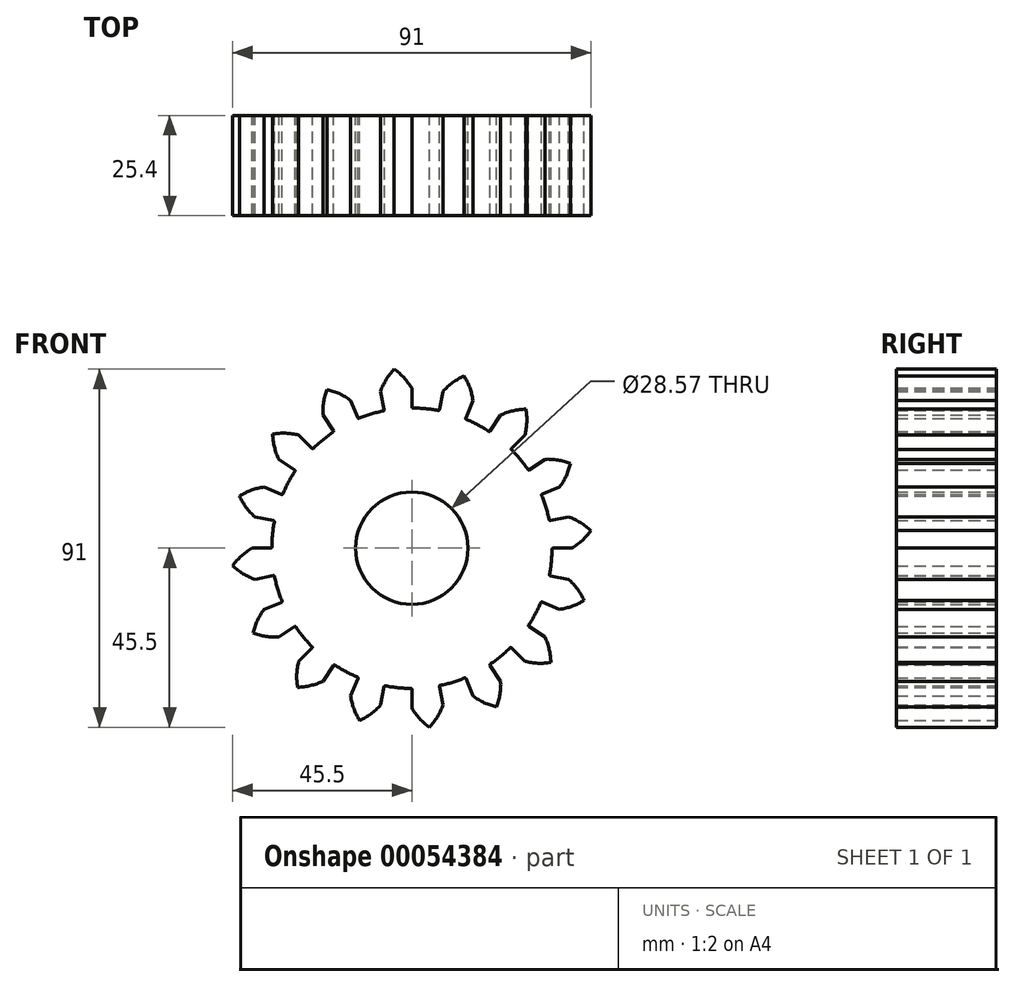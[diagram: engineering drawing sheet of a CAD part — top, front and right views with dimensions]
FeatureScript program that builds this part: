
annotation { "Feature Type Name" : "Feature", "Feature Type Description" : "" }
export const myFeature = defineFeature(function(context is Context, id is Id, definition is map)
    precondition{}
    {
        {
            var Q0;
            Q0=qCreatedBy(makeId("Front.planeOp"),FACE);
            var sketch = newSketch(context, id + "F0", { "sketchPlane" : qUnion([Q0])});
            skArc(sketch, "E0", {"start": v(-29.7, 19.55) * mm, "mid": v(-31.36, 16.76) * mm, "end": v(-32.76, 13.84) * mm});
            skLineSegment(sketch, "E1", {"start": v(-6.94, 34.88) * mm, "end": v(-7.93, 39.86) * mm, "construction": true});
            skArc(sketch, "E2.trimOffspring", {"start": v(0, 40.64) * mm, "mid": v(-1.98, 43.3) * mm, "end": v(-4.48, 45.5) * mm});
            skLineSegment(sketch, "E3.trimOffspring", {"start": v(0, 35.56) * mm, "end": v(0, 40.64) * mm, "construction": true});
            skPoint(sketch, "E4.orphan", {"position": v(0, 72.8) * mm});
            skPoint(sketch, "E5.trimOffspring.end.orphan", {"position": v(-14.48, 72.8) * mm});
            skPoint(sketch, "E6.orphan", {"position": v(-81.45, 40.64) * mm});
            skPoint(sketch, "E7.orphan", {"position": v(-81.45, 11) * mm});
            skArc(sketch, "E8", {"start": v(-20, 29.47) * mm, "mid": v(-22.6, 27.53) * mm, "end": v(-25, 25.36) * mm});
            skLineSegment(sketch, "E9", {"start": v(0, 40.64) * mm, "end": v(0, 35.56) * mm});
            skArc(sketch, "E10.MirrorCS", {"start": v(-7.93, 39.86) * mm, "mid": v(-6.5, 42.86) * mm, "end": v(-4.48, 45.5) * mm});
            skLineSegment(sketch, "E11.MirrorCS", {"start": v(-7.93, 39.86) * mm, "end": v(-6.94, 34.88) * mm});
            skLineSegment(sketch, "E12.trimOffspring", {"start": v(-7.63, 40.64) * mm, "end": v(-8.08, 40.64) * mm, "construction": true});
            skLineSegment(sketch, "E13", {"start": v(-7.93, 39.86) * mm, "end": v(-7, 35.18) * mm});
            skLineSegment(sketch, "E14", {"start": v(0, 40.64) * mm, "end": v(0, 35.87) * mm});
            skArc(sketch, "E15.1.0", {"start": v(-15.55, 37.55) * mm, "mid": v(-18.4, 39.25) * mm, "end": v(-21.55, 40.32) * mm});
            skLineSegment(sketch, "E15.1.1", {"start": v(-15.55, 37.55) * mm, "end": v(-13.73, 33.14) * mm});
            skLineSegment(sketch, "E15.1.2", {"start": v(-22.58, 33.8) * mm, "end": v(-19.93, 29.82) * mm});
            skArc(sketch, "E15.1.3", {"start": v(-22.58, 33.8) * mm, "mid": v(-22.4, 37.11) * mm, "end": v(-21.55, 40.32) * mm});
            skArc(sketch, "E15.2.0", {"start": v(-28.74, 28.74) * mm, "mid": v(-32.03, 29.22) * mm, "end": v(-35.34, 29) * mm});
            skLineSegment(sketch, "E15.2.1", {"start": v(-28.74, 28.74) * mm, "end": v(-25.36, 25.36) * mm});
            skLineSegment(sketch, "E15.2.2", {"start": v(-33.8, 22.58) * mm, "end": v(-29.78, 19.9) * mm});
            skArc(sketch, "E15.2.3", {"start": v(-33.8, 22.58) * mm, "mid": v(-34.9, 25.7) * mm, "end": v(-35.34, 29) * mm});
            skArc(sketch, "E15.3.0", {"start": v(-37.55, 15.55) * mm, "mid": v(-40.77, 14.74) * mm, "end": v(-43.75, 13.27) * mm});
            skLineSegment(sketch, "E15.3.1", {"start": v(-37.55, 15.55) * mm, "end": v(-33.09, 13.7) * mm});
            skLineSegment(sketch, "E15.3.2", {"start": v(-39.86, 7.93) * mm, "end": v(-35.12, 6.99) * mm});
            skArc(sketch, "E15.3.3", {"start": v(-39.86, 7.93) * mm, "mid": v(-42.09, 10.4) * mm, "end": v(-43.75, 13.27) * mm});
            skArc(sketch, "E15.4.0", {"start": v(-40.64, 0) * mm, "mid": v(-43.3, -1.98) * mm, "end": v(-45.5, -4.48) * mm});
            skLineSegment(sketch, "E15.4.1", {"start": v(-40.64, 0) * mm, "end": v(-35.81, 0) * mm});
            skLineSegment(sketch, "E15.4.2", {"start": v(-39.86, -7.93) * mm, "end": v(-35.12, -6.99) * mm});
            skArc(sketch, "E15.4.3", {"start": v(-39.86, -7.93) * mm, "mid": v(-42.86, -6.5) * mm, "end": v(-45.5, -4.48) * mm});
            skArc(sketch, "E15.5.0", {"start": v(-37.55, -15.55) * mm, "mid": v(-39.25, -18.4) * mm, "end": v(-40.32, -21.55) * mm});
            skLineSegment(sketch, "E15.5.1", {"start": v(-37.55, -15.55) * mm, "end": v(-33.14, -13.73) * mm});
            skLineSegment(sketch, "E15.5.2", {"start": v(-33.8, -22.58) * mm, "end": v(-29.82, -19.93) * mm});
            skArc(sketch, "E15.5.3", {"start": v(-33.8, -22.58) * mm, "mid": v(-37.11, -22.4) * mm, "end": v(-40.32, -21.55) * mm});
            skArc(sketch, "E15.6.0", {"start": v(-28.74, -28.74) * mm, "mid": v(-29.22, -32.03) * mm, "end": v(-29, -35.34) * mm});
            skLineSegment(sketch, "E15.6.1", {"start": v(-28.74, -28.74) * mm, "end": v(-25.32, -25.32) * mm});
            skLineSegment(sketch, "E15.6.2", {"start": v(-22.58, -33.8) * mm, "end": v(-19.9, -29.78) * mm});
            skArc(sketch, "E15.6.3", {"start": v(-22.58, -33.8) * mm, "mid": v(-25.7, -34.9) * mm, "end": v(-29, -35.34) * mm});
            skArc(sketch, "E15.7.0", {"start": v(-15.55, -37.55) * mm, "mid": v(-14.74, -40.77) * mm, "end": v(-13.27, -43.75) * mm});
            skLineSegment(sketch, "E15.7.1", {"start": v(-15.55, -37.55) * mm, "end": v(-13.7, -33.09) * mm});
            skLineSegment(sketch, "E15.7.2", {"start": v(-7.93, -39.86) * mm, "end": v(-7, -35.18) * mm});
            skArc(sketch, "E15.7.3", {"start": v(-7.93, -39.86) * mm, "mid": v(-10.4, -42.09) * mm, "end": v(-13.27, -43.75) * mm});
            skArc(sketch, "E15.8.0", {"start": v(0, -40.64) * mm, "mid": v(1.98, -43.3) * mm, "end": v(4.48, -45.5) * mm});
            skLineSegment(sketch, "E15.8.1", {"start": v(0, -40.64) * mm, "end": v(0, -35.87) * mm});
            skLineSegment(sketch, "E15.8.2", {"start": v(7.93, -39.86) * mm, "end": v(7, -35.18) * mm});
            skArc(sketch, "E15.8.3", {"start": v(7.93, -39.86) * mm, "mid": v(6.5, -42.86) * mm, "end": v(4.48, -45.5) * mm});
            skArc(sketch, "E15.9.0", {"start": v(15.55, -37.55) * mm, "mid": v(18.4, -39.25) * mm, "end": v(21.55, -40.32) * mm});
            skLineSegment(sketch, "E15.9.1", {"start": v(15.55, -37.55) * mm, "end": v(13.73, -33.14) * mm});
            skLineSegment(sketch, "E15.9.2", {"start": v(22.58, -33.8) * mm, "end": v(19.9, -29.78) * mm});
            skArc(sketch, "E15.9.3", {"start": v(22.58, -33.8) * mm, "mid": v(22.4, -37.11) * mm, "end": v(21.55, -40.32) * mm});
            skArc(sketch, "E15.10.0", {"start": v(28.74, -28.74) * mm, "mid": v(32.03, -29.22) * mm, "end": v(35.34, -29) * mm});
            skLineSegment(sketch, "E15.10.1", {"start": v(28.74, -28.74) * mm, "end": v(25.32, -25.32) * mm});
            skLineSegment(sketch, "E15.10.2", {"start": v(33.8, -22.58) * mm, "end": v(29.78, -19.9) * mm});
            skArc(sketch, "E15.10.3", {"start": v(33.8, -22.58) * mm, "mid": v(34.9, -25.7) * mm, "end": v(35.34, -29) * mm});
            skArc(sketch, "E15.11.0", {"start": v(37.55, -15.55) * mm, "mid": v(40.77, -14.74) * mm, "end": v(43.75, -13.27) * mm});
            skLineSegment(sketch, "E15.11.1", {"start": v(37.55, -15.55) * mm, "end": v(33.09, -13.7) * mm});
            skLineSegment(sketch, "E15.11.2", {"start": v(39.86, -7.93) * mm, "end": v(35.18, -7) * mm});
            skArc(sketch, "E15.11.3", {"start": v(39.86, -7.93) * mm, "mid": v(42.09, -10.4) * mm, "end": v(43.75, -13.27) * mm});
            skArc(sketch, "E15.12.0", {"start": v(40.64, 0) * mm, "mid": v(43.3, 1.98) * mm, "end": v(45.5, 4.48) * mm});
            skLineSegment(sketch, "E15.12.1", {"start": v(40.64, 0) * mm, "end": v(35.87, 0) * mm});
            skLineSegment(sketch, "E15.12.2", {"start": v(39.86, 7.93) * mm, "end": v(35.18, 7) * mm});
            skArc(sketch, "E15.12.3", {"start": v(39.86, 7.93) * mm, "mid": v(42.86, 6.5) * mm, "end": v(45.5, 4.48) * mm});
            skArc(sketch, "E15.13.0", {"start": v(37.55, 15.55) * mm, "mid": v(39.25, 18.4) * mm, "end": v(40.32, 21.55) * mm});
            skLineSegment(sketch, "E15.13.1", {"start": v(37.55, 15.55) * mm, "end": v(33.14, 13.73) * mm});
            skLineSegment(sketch, "E15.13.2", {"start": v(33.8, 22.58) * mm, "end": v(29.82, 19.93) * mm});
            skArc(sketch, "E15.13.3", {"start": v(33.8, 22.58) * mm, "mid": v(37.11, 22.4) * mm, "end": v(40.32, 21.55) * mm});
            skArc(sketch, "E15.14.0", {"start": v(28.74, 28.74) * mm, "mid": v(29.22, 32.03) * mm, "end": v(29, 35.34) * mm});
            skLineSegment(sketch, "E15.14.1", {"start": v(28.74, 28.74) * mm, "end": v(25.32, 25.32) * mm});
            skLineSegment(sketch, "E15.14.2", {"start": v(22.58, 33.8) * mm, "end": v(19.9, 29.78) * mm});
            skArc(sketch, "E15.14.3", {"start": v(22.58, 33.8) * mm, "mid": v(25.7, 34.9) * mm, "end": v(29, 35.34) * mm});
            skArc(sketch, "E15.15.0", {"start": v(15.55, 37.55) * mm, "mid": v(14.74, 40.77) * mm, "end": v(13.27, 43.75) * mm});
            skLineSegment(sketch, "E15.15.1", {"start": v(15.55, 37.55) * mm, "end": v(13.7, 33.09) * mm});
            skLineSegment(sketch, "E15.15.2", {"start": v(7.93, 39.86) * mm, "end": v(7, 35.18) * mm});
            skArc(sketch, "E15.15.3", {"start": v(7.93, 39.86) * mm, "mid": v(10.4, 42.09) * mm, "end": v(13.27, 43.75) * mm});
            skArc(sketch, "E16.trimOffspring", {"start": v(-29.61, 19.79) * mm, "mid": v(-31.41, 16.79) * mm, "end": v(-32.9, 13.63) * mm});
            skArc(sketch, "E17.trimOffspring", {"start": v(-34.93, 6.69) * mm, "mid": v(-35.39, 3.49) * mm, "end": v(-35.56, 0.25) * mm});
            skArc(sketch, "E18.trimOffspring", {"start": v(-34.93, 6.95) * mm, "mid": v(-35.45, 3.5) * mm, "end": v(-35.62, 0) * mm});
            skArc(sketch, "E19.trimOffspring", {"start": v(-7.2, 34.88) * mm, "mid": v(-10.34, 34.08) * mm, "end": v(-13.4, 33) * mm});
            skArc(sketch, "E20.trimOffspring", {"start": v(6.7, 34.98) * mm, "mid": v(3.5, 35.45) * mm, "end": v(0.25, 35.62) * mm});
            skArc(sketch, "E21.trimOffspring", {"start": v(6.94, 34.88) * mm, "mid": v(3.49, 35.39) * mm, "end": v(0, 35.56) * mm});
            skArc(sketch, "E22.trimOffspring", {"start": v(19.79, 29.61) * mm, "mid": v(16.79, 31.41) * mm, "end": v(13.63, 32.9) * mm});
            skArc(sketch, "E23.trimOffspring", {"start": v(19.55, 29.7) * mm, "mid": v(16.76, 31.36) * mm, "end": v(13.84, 32.76) * mm});
            skArc(sketch, "E24.trimOffspring", {"start": v(29.47, 20) * mm, "mid": v(27.45, 22.7) * mm, "end": v(25.18, 25.18) * mm});
            skArc(sketch, "E25.trimOffspring", {"start": v(34.88, 7.2) * mm, "mid": v(34.08, 10.34) * mm, "end": v(33, 13.4) * mm});
            skArc(sketch, "E26.trimOffspring", {"start": v(29.57, 19.76) * mm, "mid": v(27.57, 22.46) * mm, "end": v(25.32, 24.97) * mm});
            skArc(sketch, "E27.trimOffspring", {"start": v(34.88, 6.94) * mm, "mid": v(34.03, 10.32) * mm, "end": v(32.85, 13.6) * mm});
            skArc(sketch, "E28.trimOffspring", {"start": v(34.98, -6.7) * mm, "mid": v(35.45, -3.5) * mm, "end": v(35.62, -0.25) * mm});
            skArc(sketch, "E29.trimOffspring", {"start": v(34.88, -6.94) * mm, "mid": v(35.39, -3.49) * mm, "end": v(35.56, 0) * mm});
            skArc(sketch, "E30.trimOffspring", {"start": v(29.7, -19.55) * mm, "mid": v(31.36, -16.76) * mm, "end": v(32.76, -13.84) * mm});
            skArc(sketch, "E31.trimOffspring", {"start": v(19.97, -29.43) * mm, "mid": v(22.56, -27.49) * mm, "end": v(24.97, -25.32) * mm});
            skArc(sketch, "E32.trimOffspring", {"start": v(7.2, -34.88) * mm, "mid": v(10.34, -34.08) * mm, "end": v(13.4, -33) * mm});
            skArc(sketch, "E33.trimOffspring", {"start": v(6.94, -34.88) * mm, "mid": v(10.32, -34.03) * mm, "end": v(13.6, -32.85) * mm});
            skArc(sketch, "E34.trimOffspring", {"start": v(-6.7, -34.98) * mm, "mid": v(-3.5, -35.45) * mm, "end": v(-0.25, -35.62) * mm});
            skArc(sketch, "E35.trimOffspring", {"start": v(-6.94, -34.88) * mm, "mid": v(-3.49, -35.39) * mm, "end": v(0, -35.56) * mm});
            skArc(sketch, "E36.trimOffspring", {"start": v(-19.55, -29.7) * mm, "mid": v(-16.76, -31.36) * mm, "end": v(-13.84, -32.76) * mm});
            skArc(sketch, "E37.trimOffspring", {"start": v(-29.47, -20) * mm, "mid": v(-27.45, -22.7) * mm, "end": v(-25.18, -25.18) * mm});
            skArc(sketch, "E38.trimOffspring", {"start": v(-29.57, -19.76) * mm, "mid": v(-27.57, -22.46) * mm, "end": v(-25.32, -24.97) * mm});
            skArc(sketch, "E39.trimOffspring", {"start": v(-34.83, -7.18) * mm, "mid": v(-34, -10.44) * mm, "end": v(-32.85, -13.6) * mm});
            skArc(sketch, "E40.trimOffspring", {"start": v(-34.93, -6.95) * mm, "mid": v(-34.12, -10.22) * mm, "end": v(-33, -13.4) * mm});
            skPoint(sketch, "E41.newPointA", {"position": v(-25.14, 25.14) * mm});
            skArc(sketch, "E41.filletArc", {"start": v(-25.36, 25.36) * mm, "mid": v(-25.19, 25.29) * mm, "end": v(-25, 25.36) * mm});
            skPoint(sketch, "E42.visualSharp", {"position": v(-29.57, 19.76) * mm});
            skArc(sketch, "E42.filletArc", {"start": v(-29.7, 19.55) * mm, "mid": v(-29.67, 19.74) * mm, "end": v(-29.78, 19.9) * mm});
            skPoint(sketch, "E43.visualSharp", {"position": v(-32.85, 13.6) * mm});
            skArc(sketch, "E43.filletArc", {"start": v(-33.09, 13.7) * mm, "mid": v(-32.9, 13.7) * mm, "end": v(-32.76, 13.84) * mm});
            skPoint(sketch, "E44.visualSharp", {"position": v(-34.88, 6.94) * mm});
            skArc(sketch, "E44.filletArc", {"start": v(-34.93, 6.69) * mm, "mid": v(-34.96, 6.88) * mm, "end": v(-35.12, 6.99) * mm});
            skPoint(sketch, "E45.visualSharp", {"position": v(-35.56, 0) * mm});
            skArc(sketch, "E45.filletArc", {"start": v(-35.81, 0) * mm, "mid": v(-35.63, 0.07) * mm, "end": v(-35.56, 0.25) * mm});
            skPoint(sketch, "E46.visualSharp", {"position": v(-34.88, -6.94) * mm});
            skArc(sketch, "E46.filletArc", {"start": v(-34.83, -7.18) * mm, "mid": v(-34.94, -7.02) * mm, "end": v(-35.12, -6.99) * mm});
            skPoint(sketch, "E47.newPointB", {"position": v(-32.85, -13.6) * mm});
            skArc(sketch, "E47.filletArc", {"start": v(-33.14, -13.73) * mm, "mid": v(-33, -13.6) * mm, "end": v(-33, -13.4) * mm});
            skPoint(sketch, "E48.newPointA", {"position": v(-29.57, -19.76) * mm});
            skArc(sketch, "E48.filletArc", {"start": v(-29.47, -20) * mm, "mid": v(-29.64, -19.9) * mm, "end": v(-29.82, -19.93) * mm});
            skPoint(sketch, "E49.visualSharp", {"position": v(-25.14, -25.14) * mm});
            skArc(sketch, "E49.filletArc", {"start": v(-25.32, -25.32) * mm, "mid": v(-25.25, -25.14) * mm, "end": v(-25.32, -24.97) * mm});
            skPoint(sketch, "E50.visualSharp", {"position": v(-19.76, -29.57) * mm});
            skArc(sketch, "E50.filletArc", {"start": v(-19.55, -29.7) * mm, "mid": v(-19.74, -29.67) * mm, "end": v(-19.9, -29.78) * mm});
            skPoint(sketch, "E51.visualSharp", {"position": v(-13.6, -32.85) * mm});
            skArc(sketch, "E51.filletArc", {"start": v(-13.7, -33.09) * mm, "mid": v(-13.7, -32.9) * mm, "end": v(-13.84, -32.76) * mm});
            skPoint(sketch, "E52.newPointA", {"position": v(-6.94, -34.88) * mm});
            skArc(sketch, "E52.filletArc", {"start": v(-6.7, -34.98) * mm, "mid": v(-6.9, -35.02) * mm, "end": v(-7, -35.18) * mm});
            skPoint(sketch, "E53.newPointA", {"position": v(0, -35.56) * mm});
            skArc(sketch, "E53.filletArc", {"start": v(0, -35.87) * mm, "mid": v(-0.07, -35.7) * mm, "end": v(-0.25, -35.62) * mm});
            skPoint(sketch, "E54.newPointA", {"position": v(6.94, -34.88) * mm});
            skArc(sketch, "E54.filletArc", {"start": v(7.2, -34.88) * mm, "mid": v(7.04, -35) * mm, "end": v(7, -35.18) * mm});
            skPoint(sketch, "E55.newPointB", {"position": v(13.6, -32.85) * mm});
            skArc(sketch, "E55.filletArc", {"start": v(13.73, -33.14) * mm, "mid": v(13.6, -33) * mm, "end": v(13.4, -33) * mm});
            skPoint(sketch, "E56.visualSharp", {"position": v(19.76, -29.57) * mm});
            skArc(sketch, "E56.filletArc", {"start": v(19.97, -29.43) * mm, "mid": v(19.86, -29.59) * mm, "end": v(19.9, -29.78) * mm});
            skPoint(sketch, "E57.visualSharp", {"position": v(25.14, -25.14) * mm});
            skArc(sketch, "E57.filletArc", {"start": v(25.32, -25.32) * mm, "mid": v(25.14, -25.25) * mm, "end": v(24.97, -25.32) * mm});
            skPoint(sketch, "E58.visualSharp", {"position": v(29.57, -19.76) * mm});
            skArc(sketch, "E58.filletArc", {"start": v(29.7, -19.55) * mm, "mid": v(29.67, -19.74) * mm, "end": v(29.78, -19.9) * mm});
            skPoint(sketch, "E59.visualSharp", {"position": v(32.85, -13.6) * mm});
            skArc(sketch, "E59.filletArc", {"start": v(33.09, -13.7) * mm, "mid": v(32.9, -13.7) * mm, "end": v(32.76, -13.84) * mm});
            skPoint(sketch, "E60.newPointA", {"position": v(34.88, -6.94) * mm});
            skArc(sketch, "E60.filletArc", {"start": v(34.98, -6.7) * mm, "mid": v(35.02, -6.9) * mm, "end": v(35.18, -7) * mm});
            skPoint(sketch, "E61.newPointB", {"position": v(35.56, 0) * mm});
            skArc(sketch, "E61.filletArc", {"start": v(35.87, 0) * mm, "mid": v(35.7, -0.07) * mm, "end": v(35.62, -0.25) * mm});
            skPoint(sketch, "E62.newPointA", {"position": v(34.88, 6.94) * mm});
            skArc(sketch, "E62.filletArc", {"start": v(34.88, 7.2) * mm, "mid": v(35, 7.04) * mm, "end": v(35.18, 7) * mm});
            skPoint(sketch, "E63.newPointB", {"position": v(32.85, 13.6) * mm});
            skArc(sketch, "E63.filletArc", {"start": v(33.14, 13.73) * mm, "mid": v(33, 13.6) * mm, "end": v(33, 13.4) * mm});
            skPoint(sketch, "E64.newPointA", {"position": v(29.57, 19.76) * mm});
            skArc(sketch, "E64.filletArc", {"start": v(29.47, 20) * mm, "mid": v(29.64, 19.9) * mm, "end": v(29.82, 19.93) * mm});
            skPoint(sketch, "E65.visualSharp", {"position": v(25.14, 25.14) * mm});
            skArc(sketch, "E65.filletArc", {"start": v(25.32, 25.32) * mm, "mid": v(25.25, 25.14) * mm, "end": v(25.32, 24.97) * mm});
            skPoint(sketch, "E66.visualSharp", {"position": v(19.76, 29.57) * mm});
            skArc(sketch, "E66.filletArc", {"start": v(19.55, 29.7) * mm, "mid": v(19.74, 29.67) * mm, "end": v(19.9, 29.78) * mm});
            skPoint(sketch, "E67.visualSharp", {"position": v(13.6, 32.85) * mm});
            skArc(sketch, "E67.filletArc", {"start": v(13.7, 33.09) * mm, "mid": v(13.7, 32.9) * mm, "end": v(13.84, 32.76) * mm});
            skPoint(sketch, "E68.newPointA", {"position": v(6.94, 34.88) * mm});
            skArc(sketch, "E68.filletArc", {"start": v(6.7, 34.98) * mm, "mid": v(6.9, 35.02) * mm, "end": v(7, 35.18) * mm});
            skPoint(sketch, "E69.newPointA", {"position": v(0, 35.56) * mm});
            skArc(sketch, "E69.filletArc", {"start": v(0, 35.87) * mm, "mid": v(0.07, 35.7) * mm, "end": v(0.25, 35.62) * mm});
            skArc(sketch, "E70.filletArc", {"start": v(-7.2, 34.88) * mm, "mid": v(-7.04, 35) * mm, "end": v(-7, 35.18) * mm});
            skPoint(sketch, "E71.newPointA", {"position": v(-13.6, 32.85) * mm});
            skArc(sketch, "E71.filletArc", {"start": v(-13.73, 33.14) * mm, "mid": v(-13.6, 33) * mm, "end": v(-13.4, 33) * mm});
            skPoint(sketch, "E72.newPointA", {"position": v(-19.76, 29.57) * mm});
            skArc(sketch, "E72.filletArc", {"start": v(-20, 29.47) * mm, "mid": v(-19.9, 29.64) * mm, "end": v(-19.93, 29.82) * mm});
            skCircle(sketch, "E73", {"center": v(0, 0) * mm, "radius": 14.29 * mm});
            skSolve(sketch);
        }
        {
            var Q0;
            {var subQ52=sQuery(id+"F0.wireOp",EDGE,"E0");Q0=makeQuery(id+"F0.imprint","IMPRINT",FACE,{"disambiguationData":[TD([[makeQuery(id+"F0.imprint","IMPRINT",EDGE,{"derivedFrom":subQ52}),1.0]])]});}
            extrude(context, id + "F1", {"entities" : qUnion([Q0]), "depth" : 25.4 * mm});
        }
    });
